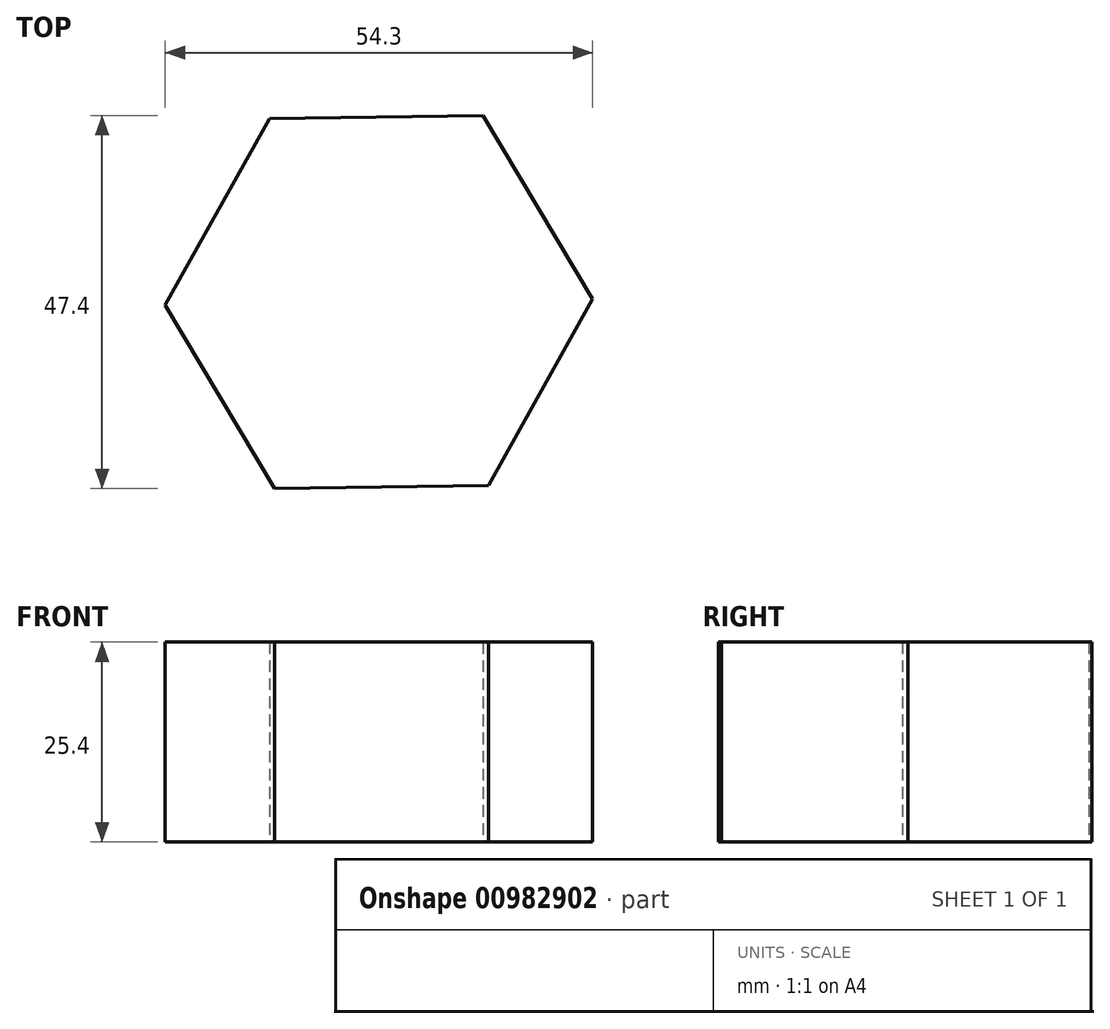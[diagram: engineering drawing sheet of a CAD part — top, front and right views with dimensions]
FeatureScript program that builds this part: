
annotation { "Feature Type Name" : "Feature", "Feature Type Description" : "" }
export const myFeature = defineFeature(function(context is Context, id is Id, definition is map)
    precondition{}
    {
        {
            var Q0;
            Q0=qCreatedBy(makeId("Top.planeOp"),FACE);
            var sketch = newSketch(context, id + "F0", { "sketchPlane" : qUnion([Q0])});
            skCircle(sketch, "E0.cCircle", {"center": v(0, 0) * mm, "radius": 27.15 * mm, "construction": true});
            skLineSegment(sketch, "E0.0", {"start": v(-13.9, 23.33) * mm, "end": v(13.25, 23.7) * mm});
            skLineSegment(sketch, "E0.1", {"start": v(13.25, 23.7) * mm, "end": v(27.15, 0.37) * mm});
            skLineSegment(sketch, "E0.2", {"start": v(27.15, 0.37) * mm, "end": v(13.9, -23.33) * mm});
            skLineSegment(sketch, "E0.3", {"start": v(13.9, -23.33) * mm, "end": v(-13.25, -23.7) * mm});
            skLineSegment(sketch, "E0.4", {"start": v(-13.25, -23.7) * mm, "end": v(-27.15, -0.37) * mm});
            skLineSegment(sketch, "E0.5", {"start": v(-27.15, -0.37) * mm, "end": v(-13.9, 23.33) * mm});
            skSolve(sketch);
        }
        {
            var Q0;
            Q0=makeQuery(id+"F0.imprint","IMPRINT",FACE,{"disambiguationData":[TD([[makeQuery(id+"F0.imprint","IMPRINT",EDGE,{"derivedFrom":sQuery(id+"F0.wireOp",EDGE,"E0.0")}),-1.0]])]});
            extrude(context, id + "F1", {"entities" : qUnion([Q0]), "depth" : 25.4 * mm, "offsetDistance" : 25.4 * mm});
        }
    });
